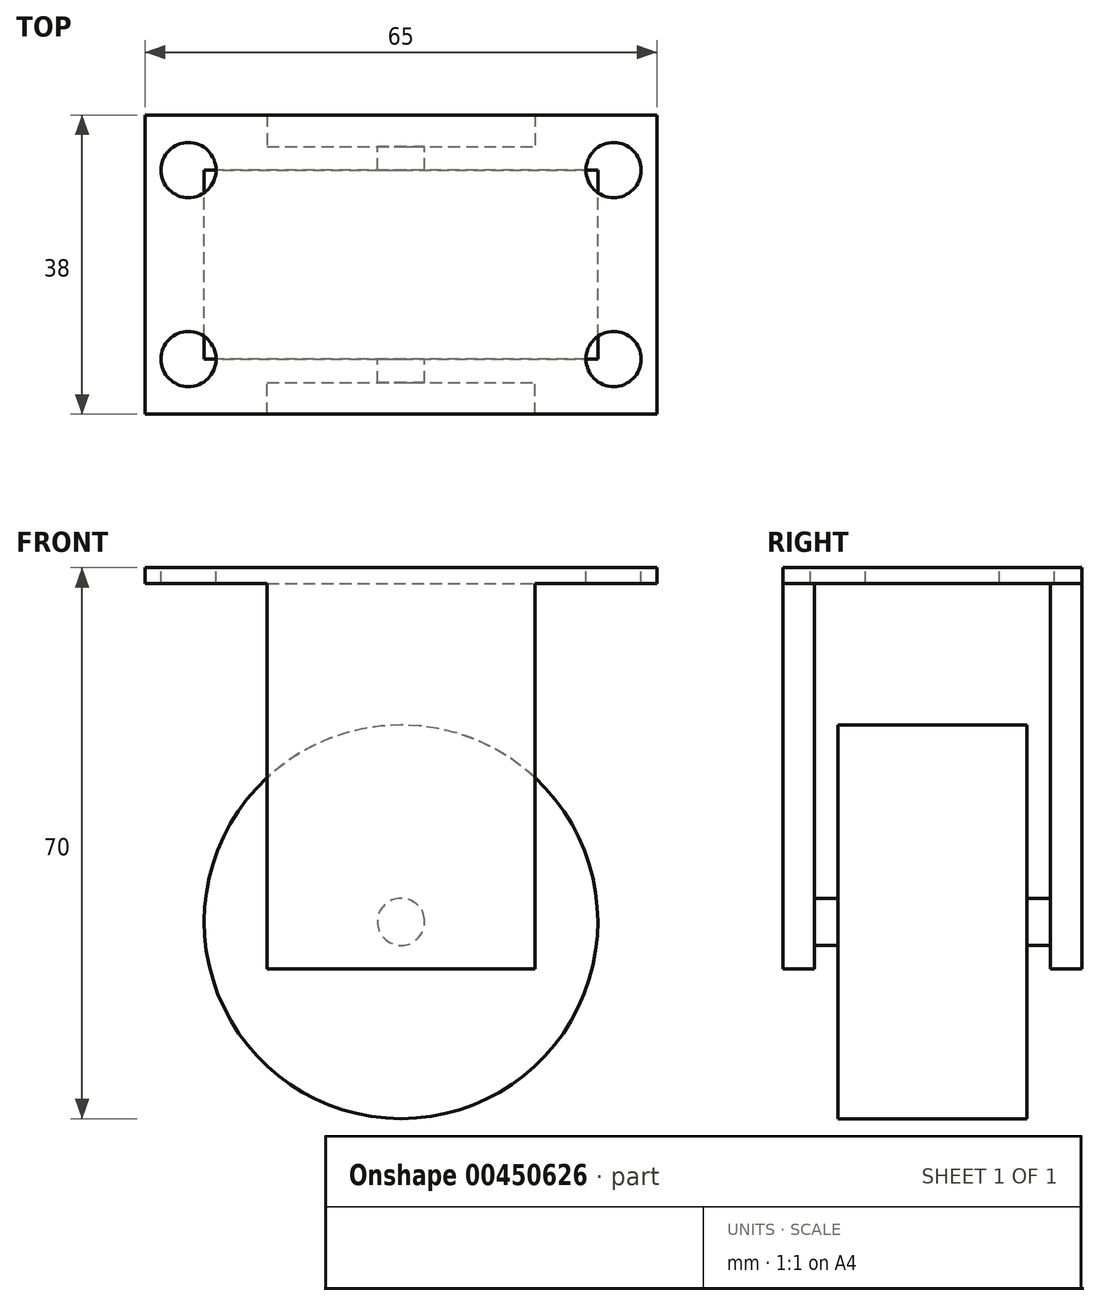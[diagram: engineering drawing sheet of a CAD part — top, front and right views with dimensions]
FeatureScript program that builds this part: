
annotation { "Feature Type Name" : "Feature", "Feature Type Description" : "" }
export const myFeature = defineFeature(function(context is Context, id is Id, definition is map)
    precondition{}
    {
        {
            var Q0;
            Q0=qCreatedBy(makeId("Top.planeOp"),FACE);
            var sketch = newSketch(context, id + "F0", { "sketchPlane" : qUnion([Q0])});
            skLineSegment(sketch, "E0.bottom", {"start": v(-32.5, 19) * mm, "end": v(32.5, 19) * mm});
            skLineSegment(sketch, "E0.top", {"start": v(-32.5, -19) * mm, "end": v(32.5, -19) * mm});
            skLineSegment(sketch, "E0.left", {"start": v(-32.5, 19) * mm, "end": v(-32.5, -19) * mm});
            skLineSegment(sketch, "E0.right", {"start": v(32.5, 19) * mm, "end": v(32.5, -19) * mm});
            skSolve(sketch);
        }
        {
            var Q0;
            Q0 = qSketchRegion(id + "F0", true);
            extrude(context, id + "F1", {"entities" : qUnion([Q0]), "depth" : 2 * mm});
        }
        {
            var Q0;
            Q0=makeQuery(id+"F1.opExtrude","CAP_FACE",FACE,{"disambiguationData":[OSD([sQuery(id+"F0.wireOp",EDGE,"E0.bottom"),sQuery(id+"F0.wireOp",EDGE,"E0.top"),sQuery(id+"F0.wireOp",EDGE,"E0.left"),sQuery(id+"F0.wireOp",EDGE,"E0.right")])],"isStart":true});
            var sketch = newSketch(context, id + "F2", { "sketchPlane" : qUnion([Q0])});
            skLineSegment(sketch, "E1.bottom", {"start": v(-17, 19) * mm, "end": v(17, 19) * mm});
            skLineSegment(sketch, "E1.top", {"start": v(-17, 15) * mm, "end": v(17, 15) * mm});
            skLineSegment(sketch, "E1.left", {"start": v(-17, 19) * mm, "end": v(-17, 15) * mm});
            skLineSegment(sketch, "E1.right", {"start": v(17, 19) * mm, "end": v(17, 15) * mm});
            skLineSegment(sketch, "E2.bottom", {"start": v(-17, -19) * mm, "end": v(17, -19) * mm});
            skLineSegment(sketch, "E2.top", {"start": v(-17, -15) * mm, "end": v(17, -15) * mm});
            skLineSegment(sketch, "E2.left", {"start": v(-17, -19) * mm, "end": v(-17, -15) * mm});
            skLineSegment(sketch, "E2.right", {"start": v(17, -19) * mm, "end": v(17, -15) * mm});
            skSolve(sketch);
        }
        {
            var Q0;
            Q0 = qSketchRegion(id + "F2", true);
            extrude(context, id + "F3", {"entities" : qUnion([Q0]), "operationType" : NewBodyOperationType.ADD, "depth" : 48.95 * mm});
        }
        {
            var Q0;
            Q0=qCreatedBy(makeId("Front.planeOp"),FACE);
            var sketch = newSketch(context, id + "F4", { "sketchPlane" : qUnion([Q0])});
            skLineSegment(sketch, "E3", {"start": v(-68.2, -43) * mm, "end": v(68.2, -43) * mm, "construction": true});
            skCircle(sketch, "E4", {"center": v(0, -43) * mm, "radius": 25 * mm});
            skSolve(sketch);
        }
        {
            var Q0;
            Q0=makeQuery(id+"F1.opExtrude","CAP_FACE",FACE,{"disambiguationData":[OSD([sQuery(id+"F0.wireOp",EDGE,"E0.bottom"),sQuery(id+"F0.wireOp",EDGE,"E0.top"),sQuery(id+"F0.wireOp",EDGE,"E0.left"),sQuery(id+"F0.wireOp",EDGE,"E0.right")])],"isStart":false});
            var sketch = newSketch(context, id + "F5", { "sketchPlane" : qUnion([Q0])});
            skLineSegment(sketch, "E5", {"start": v(27, 46.9) * mm, "end": v(27, -61.22) * mm, "construction": true});
            skLineSegment(sketch, "E6", {"start": v(-27, 42.53) * mm, "end": v(-27, -59.97) * mm, "construction": true});
            skLineSegment(sketch, "E7", {"start": v(43.44, 12) * mm, "end": v(-46.81, 12) * mm, "construction": true});
            skLineSegment(sketch, "E8", {"start": v(43.19, -12) * mm, "end": v(-46.81, -12) * mm, "construction": true});
            skCircle(sketch, "E9", {"center": v(27, 12) * mm, "radius": 3.5 * mm});
            skCircle(sketch, "E10", {"center": v(27, -12) * mm, "radius": 3.5 * mm});
            skCircle(sketch, "E11", {"center": v(-27, -12) * mm, "radius": 3.5 * mm});
            skCircle(sketch, "E12", {"center": v(-27, 12) * mm, "radius": 3.5 * mm});
            skSolve(sketch);
        }
        {
            var Q0;
            Q0 = qSketchRegion(id + "F5", true);
            extrude(context, id + "F6", {"entities" : qUnion([Q0]), "operationType" : NewBodyOperationType.REMOVE, "oppositeDirection" : true, "depth" : 3000 * mm});
        }
        {
            var Q0;
            Q0 = qSketchRegion(id + "F4", true);
            extrude(context, id + "F7", {"entities" : qUnion([Q0]), "endBound" : BoundingType.SYMMETRIC, "depth" : 24 * mm});
        }
        {
            var Q0;
            Q0=makeQuery(id+"F7.opExtrude","SWEPT_BODY",BODY,{"disambiguationData":[OSD([sQuery(id+"F4.wireOp",EDGE,"E4")])]});
            deleteBodies(context, id + "F8", {"entities" : qUnion([Q0])});
        }
        {
            var Q0;
            Q0=makeQuery(id+"F3.boolean.opBoolean","MERGE",FACE,{"derivedFrom":[makeQuery(id+"F1.opExtrude","SWEPT_FACE",FACE,{"disambiguationData":[OSD([sQuery(id+"F0.wireOp",EDGE,"E0.bottom")])]}),makeQuery(id+"F3.opExtrude","SWEPT_FACE",FACE,{"disambiguationData":[OSD([sQuery(id+"F2.wireOp",EDGE,"E2.bottom")])]})]});
            var sketch = newSketch(context, id + "F9", { "sketchPlane" : qUnion([Q0])});
            skPoint(sketch, "E13", {"position": v(0, -43) * mm});
            skCircle(sketch, "E14", {"center": v(0, -43) * mm, "radius": 3 * mm});
            skSolve(sketch);
        }
        {
            var Q0;
            Q0 = qSketchRegion(id + "F9", true);
            extrude(context, id + "F10", {"entities" : qUnion([Q0]), "operationType" : NewBodyOperationType.ADD, "oppositeDirection" : true, "depth" : 38 * mm});
        }
        {
            var Q0;
            Q0=qCreatedBy(makeId("Front.planeOp"),FACE);
            var sketch = newSketch(context, id + "F11", { "sketchPlane" : qUnion([Q0])});
            skCircle(sketch, "E15", {"center": v(0, -43) * mm, "radius": 25 * mm});
            skSolve(sketch);
        }
        {
            var Q0;
            Q0 = qSketchRegion(id + "F11", true);
            extrude(context, id + "F12", {"entities" : qUnion([Q0]), "operationType" : NewBodyOperationType.ADD, "depth" : 12 * mm, "hasSecondDirection" : true, "secondDirectionOppositeDirection" : true, "secondDirectionDepth" : 12 * mm});
        }
    });
